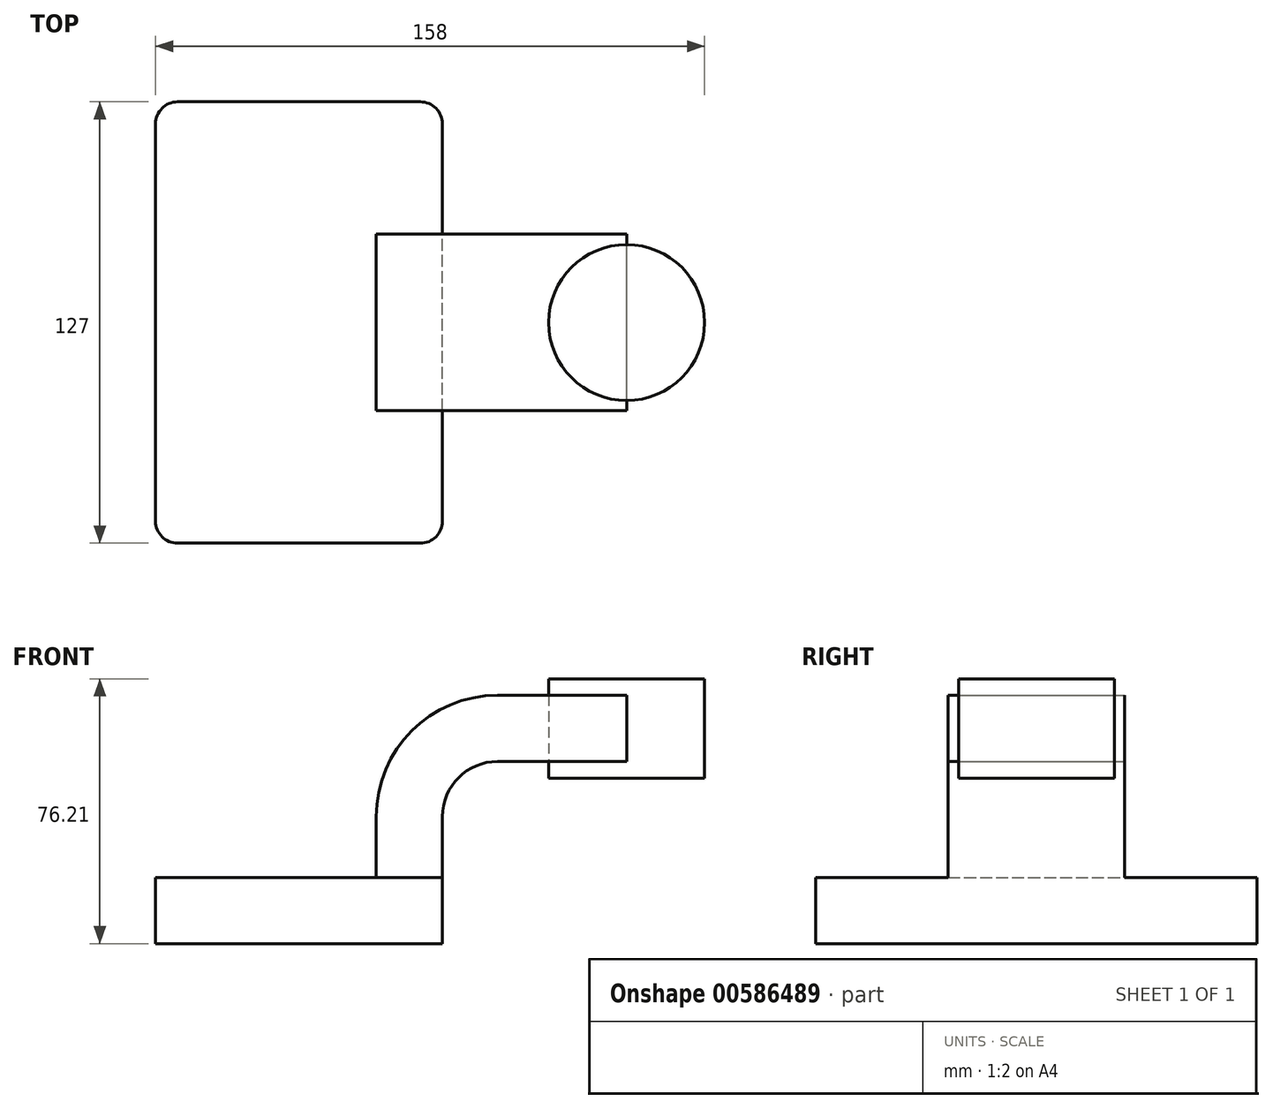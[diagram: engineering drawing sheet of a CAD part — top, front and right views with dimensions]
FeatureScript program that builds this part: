
annotation { "Feature Type Name" : "Feature", "Feature Type Description" : "" }
export const myFeature = defineFeature(function(context is Context, id is Id, definition is map)
    precondition{}
    {
        {
            var Q0;
            Q0=qCreatedBy(makeId("Front.planeOp"),FACE);
            var sketch = newSketch(context, id + "F0", { "sketchPlane" : qUnion([Q0])});
            skLineSegment(sketch, "E0.bottom", {"start": v(-41.28, -9.53) * mm, "end": v(41.28, -9.53) * mm});
            skLineSegment(sketch, "E0.top", {"start": v(-41.28, 9.52) * mm, "end": v(41.28, 9.52) * mm});
            skLineSegment(sketch, "E0.left", {"start": v(-41.28, -9.53) * mm, "end": v(-41.28, 9.52) * mm});
            skLineSegment(sketch, "E0.right", {"start": v(41.28, -9.53) * mm, "end": v(41.28, 9.52) * mm});
            skPoint(sketch, "E0.middle", {"position": v(0, 0) * mm});
            skLineSegment(sketch, "E1.bottom", {"start": v(65.93, 38.1) * mm, "end": v(116.73, 38.1) * mm});
            skLineSegment(sketch, "E1.top", {"start": v(65.93, 66.67) * mm, "end": v(116.73, 66.67) * mm});
            skLineSegment(sketch, "E1.left", {"start": v(65.93, 38.1) * mm, "end": v(65.93, 66.67) * mm});
            skLineSegment(sketch, "E1.right", {"start": v(116.73, 38.1) * mm, "end": v(116.73, 66.67) * mm});
            skPoint(sketch, "E1.middle", {"position": v(91.33, 52.39) * mm});
            skLineSegment(sketch, "E2", {"start": v(41.27, 9.52) * mm, "end": v(41.27, 27) * mm});
            skArc(sketch, "E3", {"start": v(41.27, 27) * mm, "mid": v(45.92, 38.23) * mm, "end": v(57.15, 42.88) * mm});
            skLineSegment(sketch, "E4", {"start": v(57.15, 42.88) * mm, "end": v(94.29, 42.88) * mm});
            skLineSegment(sketch, "E5.0", {"start": v(57.15, 61.93) * mm, "end": v(94.29, 61.93) * mm});
            skArc(sketch, "E5.1", {"start": v(22.22, 27) * mm, "mid": v(32.45, 51.7) * mm, "end": v(57.15, 61.93) * mm});
            skLineSegment(sketch, "E5.2", {"start": v(22.22, 9.52) * mm, "end": v(22.22, 27) * mm});
            skLineSegment(sketch, "E6", {"start": v(94.29, 38.1) * mm, "end": v(94.29, 66.67) * mm});
            skFitSpline(sketch, "E7", {"points": [v(-41.28, 9.53) * mm, v(57.15, 61.93) * mm], "startDerivative": vector(1.8, 68.2) * mm, "endDerivative": vector(118.49, -6.67) * mm});
            skSolve(sketch);
        }
        {
            var Q0;
            Q0=makeQuery(id+"F0.imprint","IMPRINT",FACE,{"disambiguationData":[TD([[makeQuery(id+"F0.imprint","IMPRINT",EDGE,{"derivedFrom":sQuery(id+"F0.wireOp",EDGE,"E0.bottom")}),1.0]])]});
            extrude(context, id + "F1", {"entities" : qUnion([Q0]), "endBound" : BoundingType.SYMMETRIC, "depth" : 127 * mm, "offsetDistance" : 25.4 * mm});
        }
        {
            var Q0;
            {var subQ1=sQuery(id+"F0.wireOp",EDGE,"E2");Q0=makeQuery(id+"F0.imprint","IMPRINT",FACE,{"disambiguationData":[TD([[makeQuery(id+"F0.imprint","IMPRINT",EDGE,{"derivedFrom":subQ1}),1.0]])]});}
            var Q1;
            {var subQ0=sQuery(id+"F0.wireOp",EDGE,"E4");var subQ1=sQuery(id+"F0.wireOp",EDGE,"E1.left");var subQ2=makeQuery(id+"F0.imprint","INTERSECT",VERTEX,{"derivedFrom":[subQ1,subQ0]});Q1=makeQuery(id+"F0.imprint","IMPRINT",FACE,{"disambiguationData":[TD([[makeQuery(id+"F0.imprint","IMPRINT",EDGE,{"disambiguationData":[TD([[subQ2,-1.0]])],"derivedFrom":subQ1}),-1.0]])]});}
            extrude(context, id + "F2", {"entities" : qUnion([Q0, Q1]), "operationType" : NewBodyOperationType.ADD, "endBound" : BoundingType.SYMMETRIC, "depth" : 50.8 * mm, "offsetDistance" : 25.4 * mm});
        }
        {
            var Q0;
            Q0=makeQuery(id+"F0.imprint","IMPRINT",FACE,{"disambiguationData":[TD([[makeQuery(id+"F0.imprint","IMPRINT",EDGE,{"derivedFrom":sQuery(id+"F0.wireOp",EDGE,"E5.1")}),1.0]])]});
            extrude(context, id + "F3", {"entities" : qUnion([Q0]), "operationType" : NewBodyOperationType.ADD, "endBound" : BoundingType.SYMMETRIC, "depth" : 15.88 * mm, "offsetDistance" : 25.4 * mm});
        }
        {
            var Q0;
            {var subQ0=sQuery(id+"F0.wireOp",EDGE,"E1.right");Q0=makeQuery(id+"F0.imprint","IMPRINT",FACE,{"disambiguationData":[TD([[makeQuery(id+"F0.imprint","IMPRINT",EDGE,{"derivedFrom":subQ0}),1.0]])]});}
            var Q1;
            Q1=sQuery(id+"F0.wireOp",EDGE,"E6");
            revolve(context, id + "F4", {"entities" : qUnion([Q0]), "axis" : qUnion([Q1]), "revolveType" : RevolveType.FULL});
        }
        {
            var Q0;
            Q0=makeQuery(id+"F1.opExtrude","CAP_EDGE",EDGE,{"disambiguationData":[OSD([sQuery(id+"F0.wireOp",EDGE,"E0.right")])],"isStart":false});
            var Q1;
            Q1=makeQuery(id+"F1.opExtrude","CAP_EDGE",EDGE,{"disambiguationData":[OSD([sQuery(id+"F0.wireOp",EDGE,"E0.left")])],"isStart":false});
            var Q2;
            Q2=makeQuery(id+"F1.opExtrude","CAP_EDGE",EDGE,{"disambiguationData":[OSD([sQuery(id+"F0.wireOp",EDGE,"E0.right")])],"isStart":true});
            var Q3;
            Q3=makeQuery(id+"F1.opExtrude","CAP_EDGE",EDGE,{"disambiguationData":[OSD([sQuery(id+"F0.wireOp",EDGE,"E0.left")])],"isStart":true});
            fillet(context, id + "F5", {"entities" : qUnion([Q0, Q1, Q2, Q3]), "radius" : 6.35 * mm, "tangentPropagation" : true, "allowEdgeOverflow" : false});
        }
    });
